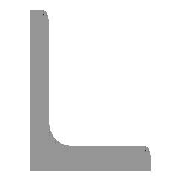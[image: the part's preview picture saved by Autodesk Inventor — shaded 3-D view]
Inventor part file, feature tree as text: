
AUTODESK INVENTOR PART (.ipt)
format: ipt  version: 2024.1 (Build 281209000, 209)  size: 120,320 bytes
history: native  units: mm (DEFAULTED — no unit token found)
features: other x4, sketch x1, plane x1
ambient origin geometry x8: Origin, YZ Plane, XZ Plane, XY Plane, X Axis, Y Axis, Z Axis, Center Point
bodies: Solid1 (feature_tree), Body (feature_tree)
feature tree (6):
  parser-record x1  (decoder bookkeeping rows leaked as tree rows — omitted from the tree; the rows remain in map.json)
  other  "Driven Length"
  other  "Start Plane"
  other  "End Plane"
  sketch  "Sketch3"  dims[d0=25.4mm d1=25.4mm d2=3.175mm d3=3.175mm d4=800.0mm d5=0.0mm d10=0.0mm d11=0.0mm d12=-0.0mm d13=800.0mm d14=3.302mm d15=1.524mm d16=90.0deg d17=800.0mm]
  plane  "Work Plane3"
